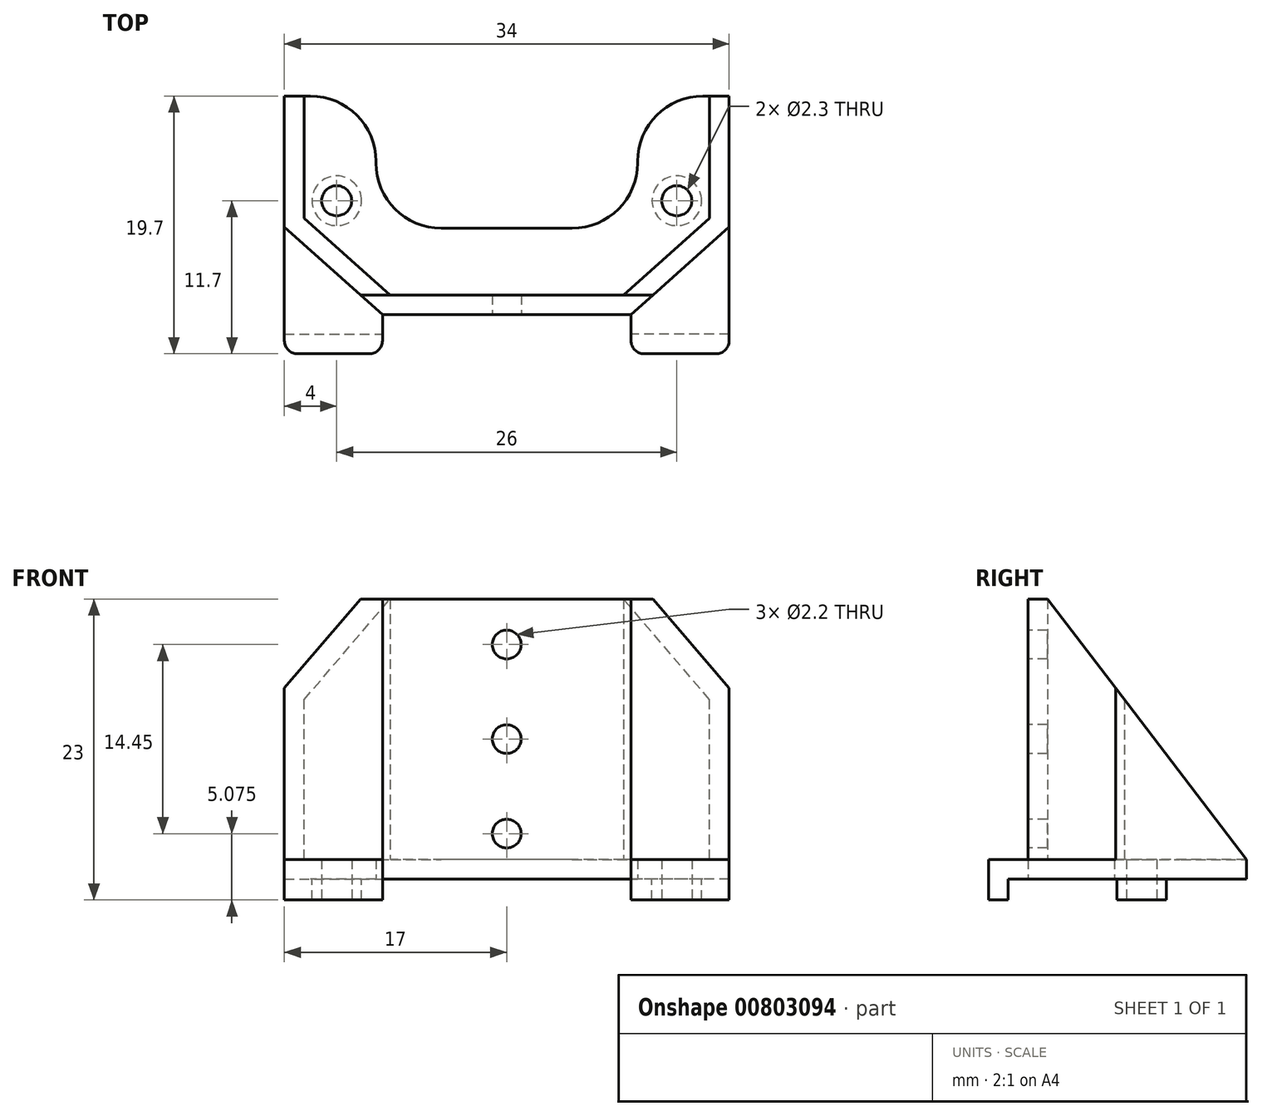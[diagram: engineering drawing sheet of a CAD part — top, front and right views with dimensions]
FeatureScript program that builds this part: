
annotation { "Feature Type Name" : "Feature", "Feature Type Description" : "" }
export const myFeature = defineFeature(function(context is Context, id is Id, definition is map)
    precondition{}
    {
        {
            var Q0;
            Q0=qCreatedBy(makeId("Top.planeOp"),FACE);
            var sketch = newSketch(context, id + "F0", { "sketchPlane" : qUnion([Q0])});
            skLineSegment(sketch, "E0", {"start": v(-15, -8.1) * mm, "end": v(15, -8.1) * mm});
            skLineSegment(sketch, "E1.bottom", {"start": v(-15, 24) * mm, "end": v(-11, 24) * mm});
            skLineSegment(sketch, "E1.top", {"start": v(-15, 0) * mm, "end": v(-11, 0) * mm});
            skLineSegment(sketch, "E1.left", {"start": v(-15, 24) * mm, "end": v(-15, 0) * mm});
            skLineSegment(sketch, "E1.right", {"start": v(-11, 24) * mm, "end": v(-11, 0) * mm});
            skLineSegment(sketch, "E2.MirrorCS", {"start": v(11, 24) * mm, "end": v(11, 0) * mm});
            skLineSegment(sketch, "E3.MirrorCS", {"start": v(15, 24) * mm, "end": v(15, 0) * mm});
            skLineSegment(sketch, "E4.MirrorCS", {"start": v(15, 24) * mm, "end": v(11, 24) * mm});
            skLineSegment(sketch, "E5.MirrorCS", {"start": v(15, 0) * mm, "end": v(11, 0) * mm});
            skSolve(sketch);
        }
        {
            var Q0;
            Q0=qCreatedBy(makeId("Top.planeOp"),FACE);
            var sketch = newSketch(context, id + "F1", { "sketchPlane" : qUnion([Q0])});
            skCircle(sketch, "E6", {"center": v(-13, 2) * mm, "radius": 1.9 * mm});
            skCircle(sketch, "E7.MirrorC", {"center": v(13, 2) * mm, "radius": 1.9 * mm});
            skLineSegment(sketch, "E8.bottom", {"start": v(-9.5, -8.2) * mm, "end": v(9.5, -8.2) * mm, "construction": true});
            skLineSegment(sketch, "E8.top", {"start": v(-9.5, -9.7) * mm, "end": v(9.5, -9.7) * mm, "construction": true});
            skLineSegment(sketch, "E8.left", {"start": v(-9.5, -8.2) * mm, "end": v(-9.5, -9.7) * mm, "construction": true});
            skLineSegment(sketch, "E8.right", {"start": v(9.5, -8.2) * mm, "end": v(9.5, -9.7) * mm, "construction": true});
            skSolve(sketch);
        }
        {
            var Q0;
            Q0=qCreatedBy(makeId("Top.planeOp"),FACE);
            var sketch = newSketch(context, id + "F2", { "sketchPlane" : qUnion([Q0])});
            skLineSegment(sketch, "E9", {"start": v(-9.5, -6.7) * mm, "end": v(-17, 0) * mm});
            skLineSegment(sketch, "E10", {"start": v(-17, 0) * mm, "end": v(-17, 10) * mm});
            skLineSegment(sketch, "E11", {"start": v(-17, 10) * mm, "end": v(-10, 10) * mm});
            skLineSegment(sketch, "E12", {"start": v(-10, 10) * mm, "end": v(-10, -0.1) * mm});
            skLineSegment(sketch, "E13", {"start": v(-10, -0.1) * mm, "end": v(0, -0.1) * mm});
            skLineSegment(sketch, "E14", {"start": v(-9.5, -6.7) * mm, "end": v(0, -6.7) * mm});
            skLineSegment(sketch, "E15.MirrorCS", {"start": v(10, -0.1) * mm, "end": v(0, -0.1) * mm});
            skLineSegment(sketch, "E16.MirrorCS", {"start": v(10, 10) * mm, "end": v(10, -0.1) * mm});
            skLineSegment(sketch, "E17.MirrorCS", {"start": v(17, 10) * mm, "end": v(10, 10) * mm});
            skLineSegment(sketch, "E18.MirrorCS", {"start": v(17, 0) * mm, "end": v(17, 10) * mm});
            skLineSegment(sketch, "E19.MirrorCS", {"start": v(9.5, -6.7) * mm, "end": v(17, 0) * mm});
            skLineSegment(sketch, "E20.MirrorCS", {"start": v(9.5, -6.7) * mm, "end": v(0, -6.7) * mm});
            skSolve(sketch);
        }
        {
            var Q0;
            Q0=makeQuery(id+"F2.imprint","IMPRINT",FACE,{"disambiguationData":[TD([[makeQuery(id+"F2.imprint","IMPRINT",EDGE,{"derivedFrom":sQuery(id+"F2.wireOp",EDGE,"E9")}),-1.0]])]});
            var sketch = newSketch(context, id + "F3", { "sketchPlane" : qUnion([Q0])});
            skLineSegment(sketch, "E21", {"start": v(-17, 10) * mm, "end": v(-17, 0) * mm});
            skLineSegment(sketch, "E22", {"start": v(-17, 0) * mm, "end": v(-9.5, -6.7) * mm});
            skLineSegment(sketch, "E23", {"start": v(-9.5, -6.7) * mm, "end": v(0, -6.7) * mm});
            skLineSegment(sketch, "E24", {"start": v(-17, 10) * mm, "end": v(-15.5, 10) * mm});
            skLineSegment(sketch, "E25", {"start": v(-15.5, 10) * mm, "end": v(-15.5, 0.67) * mm});
            skLineSegment(sketch, "E26", {"start": v(-15.5, 0.67) * mm, "end": v(-8.93, -5.2) * mm});
            skLineSegment(sketch, "E27", {"start": v(-8.93, -5.2) * mm, "end": v(0, -5.2) * mm});
            skPoint(sketch, "E28.orphan", {"position": v(-15.5, 0) * mm});
            skLineSegment(sketch, "E29.MirrorCS", {"start": v(15.5, 10) * mm, "end": v(15.5, 0.67) * mm});
            skLineSegment(sketch, "E30.MirrorCS", {"start": v(17, 10) * mm, "end": v(17, 0) * mm});
            skLineSegment(sketch, "E31.MirrorCS", {"start": v(17, 0) * mm, "end": v(9.5, -6.7) * mm});
            skLineSegment(sketch, "E32.MirrorCS", {"start": v(9.5, -6.7) * mm, "end": v(0, -6.7) * mm});
            skLineSegment(sketch, "E33.MirrorCS", {"start": v(8.93, -5.2) * mm, "end": v(0, -5.2) * mm});
            skLineSegment(sketch, "E34.MirrorCS", {"start": v(15.5, 0.67) * mm, "end": v(8.93, -5.2) * mm});
            skLineSegment(sketch, "E35.MirrorCS", {"start": v(17, 10) * mm, "end": v(15.5, 10) * mm});
            skSolve(sketch);
        }
        {
            var Q0;
            Q0=qSketchRegion(id+"F3",true);
            extrude(context, id + "F4", {"entities" : qUnion([Q0]), "depth" : 21.4 * mm, "offsetDistance" : 25 * mm});
        }
        {
            var Q0;
            Q0=qSketchRegion(id+"F2",true);
            extrude(context, id + "F5", {"entities" : qUnion([Q0]), "operationType" : NewBodyOperationType.ADD, "depth" : 1.5 * mm, "offsetDistance" : 25 * mm});
        }
        {
            var Q0;
            Q0=qSketchRegion(id+"F1",true);
            extrude(context, id + "F6", {"entities" : qUnion([Q0]), "operationType" : NewBodyOperationType.ADD, "oppositeDirection" : true, "depth" : 1.6 * mm, "offsetDistance" : 25 * mm});
        }
        {
            var Q0;
            Q0=qCreatedBy(makeId("Right.planeOp"),FACE);
            var sketch = newSketch(context, id + "F7", { "sketchPlane" : qUnion([Q0])});
            skLineSegment(sketch, "E36", {"start": v(10, 1.5) * mm, "end": v(-5.2, 21.4) * mm});
            skLineSegment(sketch, "E37", {"start": v(-5.2, 21.4) * mm, "end": v(10, 21.4) * mm});
            skLineSegment(sketch, "E38", {"start": v(10, 21.4) * mm, "end": v(10, 1.5) * mm});
            skSolve(sketch);
        }
        {
            var Q0;
            Q0=qSketchRegion(id+"F7",true);
            extrude(context, id + "F8", {"entities" : qUnion([Q0]), "operationType" : NewBodyOperationType.REMOVE, "endBound" : BoundingType.THROUGH_ALL, "oppositeDirection" : true, "depth" : 25 * mm, "offsetDistance" : 25 * mm, "hasSecondDirection" : true, "secondDirectionBound" : SecondDirectionBoundingType.THROUGH_ALL, "secondDirectionOppositeDirection" : false, "secondDirectionDepth" : 25 * mm});
        }
        {
            var Q0;
            Q0=qCreatedBy(makeId("Top.planeOp"),FACE);
            var sketch = newSketch(context, id + "F9", { "sketchPlane" : qUnion([Q0])});
            skCircle(sketch, "E39", {"center": v(13, 2) * mm, "radius": 1.15 * mm});
            skCircle(sketch, "E40.MirrorC", {"center": v(-13, 2) * mm, "radius": 1.15 * mm});
            skSolve(sketch);
        }
        {
            var Q0;
            Q0=qSketchRegion(id+"F9",true);
            extrude(context, id + "F10", {"entities" : qUnion([Q0]), "operationType" : NewBodyOperationType.REMOVE, "endBound" : BoundingType.THROUGH_ALL, "depth" : 25 * mm, "offsetDistance" : 25 * mm, "hasSecondDirection" : true, "secondDirectionBound" : SecondDirectionBoundingType.THROUGH_ALL, "secondDirectionOppositeDirection" : true, "secondDirectionDepth" : 25 * mm});
        }
        {
            var Q0;
            Q0=makeQuery(id+"F4.opExtrude","SWEPT_FACE",FACE,{"disambiguationData":[OSD([sQuery(id+"F3.wireOp",EDGE,"E23"),sQuery(id+"F3.wireOp",EDGE,"E32.MirrorCS")])]});
            var sketch = newSketch(context, id + "F11", { "sketchPlane" : qUnion([Q0])});
            skCircle(sketch, "E41", {"center": v(0, 3.47) * mm, "radius": 1.1 * mm});
            skCircle(sketch, "E42", {"center": v(0, 17.92) * mm, "radius": 1.1 * mm});
            skCircle(sketch, "E43", {"center": v(0, 10.7) * mm, "radius": 1.1 * mm});
            skSolve(sketch);
        }
        {
            var Q0;
            Q0=qSketchRegion(id+"F11",true);
            extrude(context, id + "F12", {"entities" : qUnion([Q0]), "operationType" : NewBodyOperationType.REMOVE, "endBound" : BoundingType.UP_TO_NEXT, "oppositeDirection" : true, "depth" : 25 * mm, "offsetDistance" : 25 * mm});
        }
        {
            var Q0;
            Q0=qCreatedBy(makeId("Top.planeOp"),FACE);
            var sketch = newSketch(context, id + "F13", { "sketchPlane" : qUnion([Q0])});
            skLineSegment(sketch, "E44.bottom", {"start": v(-17, -9.7) * mm, "end": v(-9.5, -9.7) * mm});
            skLineSegment(sketch, "E44.left", {"start": v(-17, -9.7) * mm, "end": v(-17, 0) * mm});
            skLineSegment(sketch, "E44.right", {"start": v(-9.5, -9.7) * mm, "end": v(-9.5, -6.7) * mm});
            skLineSegment(sketch, "E45.MirrorCS", {"start": v(17, -9.7) * mm, "end": v(9.5, -9.7) * mm});
            skLineSegment(sketch, "E46.MirrorCS", {"start": v(17, -9.7) * mm, "end": v(17, 0) * mm});
            skLineSegment(sketch, "E47.MirrorCS", {"start": v(9.5, -9.7) * mm, "end": v(9.5, -6.7) * mm});
            skLineSegment(sketch, "E48", {"start": v(-17, 0) * mm, "end": v(-9.5, -6.7) * mm});
            skPoint(sketch, "E49.orphan", {"position": v(-9.5, 0) * mm});
            skPoint(sketch, "E50.MirrorCS.end.orphan", {"position": v(9.5, 0) * mm});
            skPoint(sketch, "E50.MirrorCS.start.orphan", {"position": v(17, 0) * mm});
            skLineSegment(sketch, "E51.MirrorCS", {"start": v(17, 0) * mm, "end": v(9.5, -6.7) * mm});
            skSolve(sketch);
        }
        {
            var Q0;
            Q0=makeQuery(id+"F13.imprint","IMPRINT",FACE,{"disambiguationData":[TD([[makeQuery(id+"F13.imprint","IMPRINT",EDGE,{"derivedFrom":sQuery(id+"F13.wireOp",EDGE,"E44.bottom")}),1.0]])]});
            var sketch = newSketch(context, id + "F14", { "sketchPlane" : qUnion([Q0])});
            skLineSegment(sketch, "E52.bottom", {"start": v(-17, -9.7) * mm, "end": v(-9.5, -9.7) * mm});
            skLineSegment(sketch, "E52.top", {"start": v(-17, -8.2) * mm, "end": v(-9.5, -8.2) * mm});
            skLineSegment(sketch, "E52.left", {"start": v(-17, -9.7) * mm, "end": v(-17, -8.2) * mm});
            skLineSegment(sketch, "E52.right", {"start": v(-9.5, -9.7) * mm, "end": v(-9.5, -8.2) * mm});
            skLineSegment(sketch, "E53.MirrorCS", {"start": v(9.5, -9.7) * mm, "end": v(9.5, -8.2) * mm});
            skLineSegment(sketch, "E54.MirrorCS", {"start": v(17, -9.7) * mm, "end": v(17, -8.2) * mm});
            skLineSegment(sketch, "E55.MirrorCS", {"start": v(17, -8.2) * mm, "end": v(9.5, -8.2) * mm});
            skLineSegment(sketch, "E56.MirrorCS", {"start": v(17, -9.7) * mm, "end": v(9.5, -9.7) * mm});
            skSolve(sketch);
        }
        {
            var Q0;
            Q0=qSketchRegion(id+"F13",true);
            extrude(context, id + "F15", {"entities" : qUnion([Q0]), "operationType" : NewBodyOperationType.ADD, "depth" : 1.5 * mm, "offsetDistance" : 25 * mm});
        }
        {
            var Q0;
            Q0=qSketchRegion(id+"F14",true);
            extrude(context, id + "F16", {"entities" : qUnion([Q0]), "operationType" : NewBodyOperationType.ADD, "oppositeDirection" : true, "depth" : 1.6 * mm, "offsetDistance" : 25 * mm});
        }
        {
            var Q0;
            Q0=makeQuery(id+"F16.boolean.opBoolean","MERGE",EDGE,{"derivedFrom":[makeQuery(id+"F15.opExtrude","SWEPT_EDGE",EDGE,{"disambiguationData":[OSD([sQuery(id+"F13.wireOp",EDGE,"E45.MirrorCS"),sQuery(id+"F13.wireOp",EDGE,"E46.MirrorCS")])]}),makeQuery(id+"F16.opExtrude","SWEPT_EDGE",EDGE,{"disambiguationData":[OSD([sQuery(id+"F14.wireOp",EDGE,"E54.MirrorCS"),sQuery(id+"F14.wireOp",EDGE,"E56.MirrorCS")])]})]});
            var Q1;
            Q1=makeQuery(id+"F16.boolean.opBoolean","MERGE",EDGE,{"derivedFrom":[makeQuery(id+"F15.opExtrude","SWEPT_EDGE",EDGE,{"disambiguationData":[OSD([sQuery(id+"F13.wireOp",EDGE,"E44.bottom"),sQuery(id+"F13.wireOp",EDGE,"E44.left")])]}),makeQuery(id+"F16.opExtrude","SWEPT_EDGE",EDGE,{"disambiguationData":[OSD([sQuery(id+"F14.wireOp",EDGE,"E52.bottom"),sQuery(id+"F14.wireOp",EDGE,"E52.left")])]})]});
            var Q2;
            Q2=makeQuery(id+"F16.boolean.opBoolean","MERGE",EDGE,{"derivedFrom":[makeQuery(id+"F15.opExtrude","SWEPT_EDGE",EDGE,{"disambiguationData":[OSD([sQuery(id+"F13.wireOp",EDGE,"E44.bottom"),sQuery(id+"F13.wireOp",EDGE,"E44.right")])]}),makeQuery(id+"F16.opExtrude","SWEPT_EDGE",EDGE,{"disambiguationData":[OSD([sQuery(id+"F14.wireOp",EDGE,"E52.bottom"),sQuery(id+"F14.wireOp",EDGE,"E52.right")])]})]});
            var Q3;
            Q3=makeQuery(id+"F16.boolean.opBoolean","MERGE",EDGE,{"derivedFrom":[makeQuery(id+"F15.opExtrude","SWEPT_EDGE",EDGE,{"disambiguationData":[OSD([sQuery(id+"F13.wireOp",EDGE,"E45.MirrorCS"),sQuery(id+"F13.wireOp",EDGE,"E47.MirrorCS")])]}),makeQuery(id+"F16.opExtrude","SWEPT_EDGE",EDGE,{"disambiguationData":[OSD([sQuery(id+"F14.wireOp",EDGE,"E53.MirrorCS"),sQuery(id+"F14.wireOp",EDGE,"E56.MirrorCS")])]})]});
            fillet(context, id + "F17", {"entities" : qUnion([Q0, Q1, Q2, Q3]), "radius" : 1 * mm, "tangentPropagation" : true, "allowEdgeOverflow" : false});
        }
        {
            var Q0;
            Q0=makeQuery(id+"F5.opExtrude","SWEPT_EDGE",EDGE,{"disambiguationData":[OSD([sQuery(id+"F2.wireOp",EDGE,"E15.MirrorCS"),sQuery(id+"F2.wireOp",EDGE,"E16.MirrorCS")])]});
            var Q1;
            Q1=makeQuery(id+"F5.opExtrude","SWEPT_EDGE",EDGE,{"disambiguationData":[OSD([sQuery(id+"F2.wireOp",EDGE,"E16.MirrorCS"),sQuery(id+"F2.wireOp",EDGE,"E17.MirrorCS")])]});
            var Q2;
            Q2=makeQuery(id+"F5.opExtrude","SWEPT_EDGE",EDGE,{"disambiguationData":[OSD([sQuery(id+"F2.wireOp",EDGE,"E12"),sQuery(id+"F2.wireOp",EDGE,"E13")])]});
            var Q3;
            Q3=makeQuery(id+"F5.opExtrude","SWEPT_EDGE",EDGE,{"disambiguationData":[OSD([sQuery(id+"F2.wireOp",EDGE,"E11"),sQuery(id+"F2.wireOp",EDGE,"E12")])]});
            fillet(context, id + "F18", {"entities" : qUnion([Q0, Q1, Q2, Q3]), "radius" : 5 * mm, "tangentPropagation" : true, "allowEdgeOverflow" : false});
        }
    });
